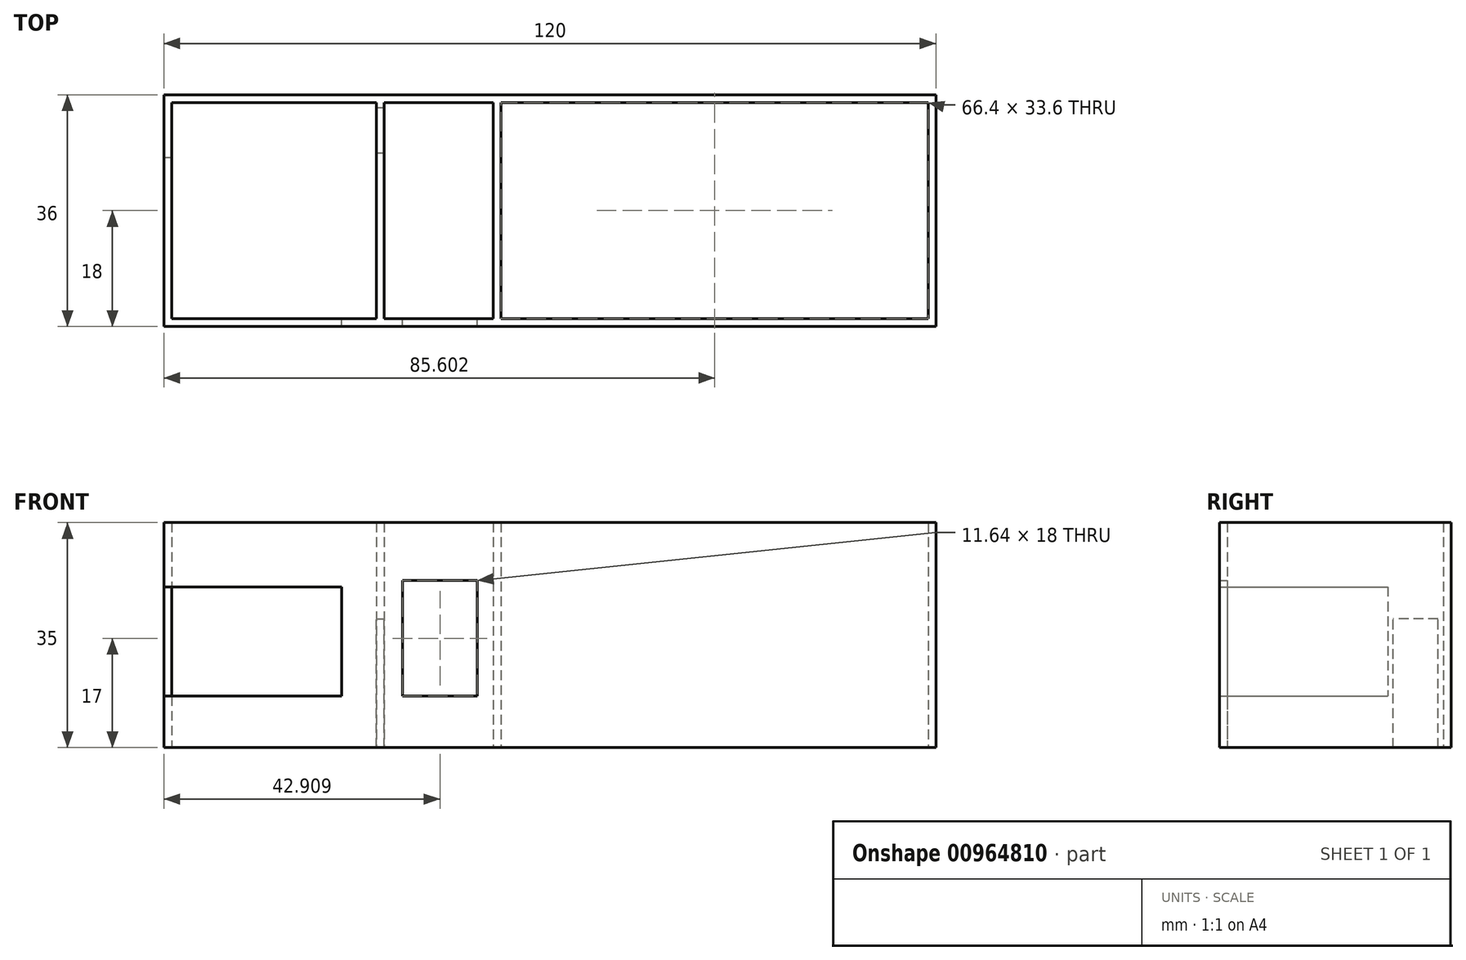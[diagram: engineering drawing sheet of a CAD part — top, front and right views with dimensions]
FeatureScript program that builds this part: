
annotation { "Feature Type Name" : "Feature", "Feature Type Description" : "" }
export const myFeature = defineFeature(function(context is Context, id is Id, definition is map)
    precondition{}
    {
        {
            var Q0;
            Q0=qCreatedBy(makeId("Top.planeOp"),FACE);
            var sketch = newSketch(context, id + "F0", { "sketchPlane" : qUnion([Q0])});
            skLineSegment(sketch, "E0.bottom", {"start": v(-115.18, 0) * mm, "end": v(4.82, 0) * mm});
            skLineSegment(sketch, "E0.top", {"start": v(-115.18, -36) * mm, "end": v(4.82, -36) * mm});
            skLineSegment(sketch, "E0.left", {"start": v(-115.18, 0) * mm, "end": v(-115.18, -36) * mm});
            skLineSegment(sketch, "E0.right", {"start": v(4.82, 0) * mm, "end": v(4.82, -36) * mm});
            skLineSegment(sketch, "E1.bottom", {"start": v(-113.98, -1.2) * mm, "end": v(3.62, -1.2) * mm});
            skLineSegment(sketch, "E1.top", {"start": v(-113.98, -34.8) * mm, "end": v(3.62, -34.8) * mm});
            skLineSegment(sketch, "E1.left", {"start": v(-113.98, -1.2) * mm, "end": v(-113.98, -34.8) * mm});
            skLineSegment(sketch, "E1.right", {"start": v(3.62, -1.2) * mm, "end": v(3.62, -34.8) * mm});
            skLineSegment(sketch, "E2.top", {"start": v(-63.98, -34.8) * mm, "end": v(-62.78, -34.8) * mm});
            skLineSegment(sketch, "E2.left", {"start": v(-63.98, -1.2) * mm, "end": v(-63.98, -34.8) * mm});
            skLineSegment(sketch, "E2.right", {"start": v(-62.78, -1.2) * mm, "end": v(-62.78, -34.8) * mm});
            skLineSegment(sketch, "E3.bottom", {"start": v(-49.02, -1.2) * mm, "end": v(-45.24, -1.2) * mm});
            skLineSegment(sketch, "E4.top", {"start": v(-82.18, -34.8) * mm, "end": v(-80.98, -34.8) * mm});
            skLineSegment(sketch, "E4.left", {"start": v(-82.18, -1.2) * mm, "end": v(-82.18, -34.8) * mm});
            skLineSegment(sketch, "E4.right", {"start": v(-80.98, -1.2) * mm, "end": v(-80.98, -34.8) * mm});
            skLineSegment(sketch, "E5.right", {"start": v(-82.18, -8.7) * mm, "end": v(-82.18, -26.7) * mm});
            skPoint(sketch, "E6", {"position": v(-80.98, -7.2) * mm});
            skPoint(sketch, "E7", {"position": v(-82.18, -7.2) * mm});
            skLineSegment(sketch, "E8.bottom", {"start": v(-107.98, -1.2) * mm, "end": v(-89.98, -1.2) * mm});
            skLineSegment(sketch, "E8.top", {"start": v(-107.98, -21.2) * mm, "end": v(-89.98, -21.2) * mm});
            skLineSegment(sketch, "E8.left", {"start": v(-107.98, -1.2) * mm, "end": v(-107.98, -21.2) * mm});
            skLineSegment(sketch, "E8.right", {"start": v(-89.98, -1.2) * mm, "end": v(-89.98, -21.2) * mm});
            skLineSegment(sketch, "E9.bottom", {"start": v(-80.98, -1.2) * mm, "end": v(-63.98, -1.2) * mm});
            skLineSegment(sketch, "E9.left", {"start": v(-80.98, -1.2) * mm, "end": v(-80.98, -8.13) * mm});
            skLineSegment(sketch, "E9.right", {"start": v(-63.98, -1.2) * mm, "end": v(-63.98, -8.13) * mm});
            skLineSegment(sketch, "E10.bottom", {"start": v(-80.98, -26.64) * mm, "end": v(-63.98, -26.64) * mm});
            skLineSegment(sketch, "E10.top", {"start": v(-80.98, -34.8) * mm, "end": v(-63.98, -34.8) * mm});
            skLineSegment(sketch, "E10.left", {"start": v(-80.98, -26.64) * mm, "end": v(-80.98, -34.8) * mm});
            skLineSegment(sketch, "E10.right", {"start": v(-63.98, -26.64) * mm, "end": v(-63.98, -34.8) * mm});
            skSolve(sketch);
        }
        {
            var Q0;
            Q0=makeQuery(id+"F0.imprint","IMPRINT",FACE,{"disambiguationData":[TD([[makeQuery(id+"F0.imprint","IMPRINT",EDGE,{"derivedFrom":sQuery(id+"F0.wireOp",EDGE,"E0.bottom")}),-1.0]])]});
            var Q1;
            {var subQ0=sQuery(id+"F0.wireOp",EDGE,"E4.left");var subQ4=makeQuery(id+"F0.imprint","IMPRINT",VERTEX,{"disambiguationData":[OD(0.0)],"derivedFrom":subQ0});Q1=makeQuery(id+"F0.imprint","IMPRINT",FACE,{"disambiguationData":[TD([[makeQuery(id+"F0.imprint","IMPRINT",EDGE,{"disambiguationData":[TD([[subQ4,-1.0]])],"derivedFrom":subQ0}),1.0]])]});}
            var Q2;
            {var subQ5=sQuery(id+"F0.wireOp",EDGE,"E2.right");Q2=makeQuery(id+"F0.imprint","IMPRINT",FACE,{"disambiguationData":[TD([[makeQuery(id+"F0.imprint","IMPRINT",EDGE,{"derivedFrom":subQ5}),-1.0]])]});}
            extrude(context, id + "F1", {"entities" : qUnion([Q0, Q1, Q2]), "depth" : 35 * mm, "offsetDistance" : 25 * mm});
        }
        {
            var Q0;
            Q0=makeQuery(id+"F1.opExtrude","SWEPT_FACE",FACE,{"disambiguationData":[OSD([sQuery(id+"F0.wireOp",EDGE,"E4.right")])]});
            var sketch = newSketch(context, id + "F2", { "sketchPlane" : qUnion([Q0])});
            skLineSegment(sketch, "E11.bottom", {"start": v(-2, 0) * mm, "end": v(-9, 0) * mm});
            skLineSegment(sketch, "E11.top", {"start": v(-2, 20) * mm, "end": v(-9, 20) * mm});
            skLineSegment(sketch, "E11.left", {"start": v(-2, 0) * mm, "end": v(-2, 20) * mm});
            skLineSegment(sketch, "E11.right", {"start": v(-9, 0) * mm, "end": v(-9, 20) * mm});
            skSolve(sketch);
        }
        {
            var Q0;
            Q0=makeQuery(id+"F2.imprint","IMPRINT",FACE,{"disambiguationData":[TD([[makeQuery(id+"F2.imprint","IMPRINT",EDGE,{"derivedFrom":sQuery(id+"F2.wireOp",EDGE,"E11.bottom")}),-1.0]])]});
            extrude(context, id + "F3", {"entities" : qUnion([Q0]), "operationType" : NewBodyOperationType.REMOVE, "oppositeDirection" : true, "depth" : 1.2 * mm, "offsetDistance" : 25 * mm});
        }
        {
            var Q0;
            {var subQ0=sQuery(id+"F0.wireOp",EDGE,"E1.top");Q0=makeQuery(id+"F1.opExtrude","SWEPT_FACE",FACE,{"disambiguationData":[OSD([subQ0]),TDD([makeQuery(id+"F0.imprint","IMPRINT",EDGE,{"disambiguationData":[TD([[makeQuery(id+"F0.imprint","INTERSECT",VERTEX,{"derivedFrom":[subQ0,sQuery(id+"F0.wireOp",EDGE,"E4.right")]}),-1.0]])],"derivedFrom":subQ0})])]});}
            var sketch = newSketch(context, id + "F4", { "sketchPlane" : qUnion([Q0])});
            skLineSegment(sketch, "E12.bottom", {"start": v(66.45, 26) * mm, "end": v(78.1, 26) * mm});
            skLineSegment(sketch, "E12.top", {"start": v(66.45, 8) * mm, "end": v(78.1, 8) * mm});
            skLineSegment(sketch, "E12.left", {"start": v(66.45, 26) * mm, "end": v(66.45, 8) * mm});
            skLineSegment(sketch, "E12.right", {"start": v(78.1, 26) * mm, "end": v(78.1, 8) * mm});
            skSolve(sketch);
        }
        {
            var Q0;
            Q0 = qSketchRegion(id + "F4", true);
            extrude(context, id + "F5", {"entities" : qUnion([Q0]), "operationType" : NewBodyOperationType.REMOVE, "endBound" : BoundingType.THROUGH_ALL, "oppositeDirection" : true, "depth" : 1.2 * mm, "offsetDistance" : 25 * mm});
        }
        {
            var Q0;
            {var subQ0=sQuery(id+"F0.wireOp",EDGE,"E1.top");Q0=makeQuery(id+"F1.opExtrude","SWEPT_FACE",FACE,{"disambiguationData":[OSD([subQ0]),TDD([makeQuery(id+"F0.imprint","IMPRINT",EDGE,{"disambiguationData":[TD([[makeQuery(id+"F0.imprint","INTERSECT",VERTEX,{"derivedFrom":[subQ0,sQuery(id+"F0.wireOp",EDGE,"E1.left")]}),-1.0]])],"derivedFrom":subQ0})])]});}
            var sketch = newSketch(context, id + "F6", { "sketchPlane" : qUnion([Q0])});
            skLineSegment(sketch, "E13.bottom", {"start": v(87.54, 25) * mm, "end": v(112.54, 25) * mm});
            skLineSegment(sketch, "E13.top", {"start": v(87.54, 8) * mm, "end": v(112.54, 8) * mm});
            skLineSegment(sketch, "E13.left", {"start": v(87.54, 25) * mm, "end": v(87.54, 8) * mm});
            skLineSegment(sketch, "E13.right", {"start": v(112.54, 25) * mm, "end": v(112.54, 8) * mm});
            skSolve(sketch);
        }
        {
            var Q0;
            Q0=makeQuery(id+"F6.imprint","IMPRINT",FACE,{"disambiguationData":[TD([[makeQuery(id+"F6.imprint","IMPRINT",EDGE,{"derivedFrom":sQuery(id+"F6.wireOp",EDGE,"E13.bottom")}),-1.0]])]});
            extrude(context, id + "F7", {"entities" : qUnion([Q0]), "operationType" : NewBodyOperationType.REMOVE, "oppositeDirection" : true, "depth" : 1.2 * mm, "offsetDistance" : 25 * mm});
        }
        {
            var Q0;
            Q0=makeQuery(id+"F7.boolean.opBoolean","COPY",FACE,{"derivedFrom":makeQuery(id+"F7.opExtrude","SWEPT_FACE",FACE,{"disambiguationData":[OSD([sQuery(id+"F6.wireOp",EDGE,"E13.right")])]})});
            var sketch = newSketch(context, id + "F8", { "sketchPlane" : qUnion([Q0])});
            skLineSegment(sketch, "E14.bottom", {"start": v(-36, 25) * mm, "end": v(-34.8, 25) * mm});
            skLineSegment(sketch, "E14.top", {"start": v(-36, 8) * mm, "end": v(-34.8, 8) * mm});
            skLineSegment(sketch, "E14.left", {"start": v(-36, 25) * mm, "end": v(-36, 8) * mm});
            skLineSegment(sketch, "E14.right", {"start": v(-34.8, 25) * mm, "end": v(-34.8, 8) * mm});
            skSolve(sketch);
        }
        {
            var Q0;
            Q0=makeQuery(id+"F8.imprint","IMPRINT",FACE,{"disambiguationData":[TD([[makeQuery(id+"F8.imprint","IMPRINT",EDGE,{"derivedFrom":sQuery(id+"F8.wireOp",EDGE,"E14.bottom")}),-1.0]])]});
            extrude(context, id + "F9", {"entities" : qUnion([Q0]), "operationType" : NewBodyOperationType.REMOVE, "oppositeDirection" : true, "depth" : 3 * mm, "offsetDistance" : 25 * mm});
        }
        {
            var Q0;
            Q0=makeQuery(id+"F1.opExtrude","SWEPT_FACE",FACE,{"disambiguationData":[OSD([sQuery(id+"F0.wireOp",EDGE,"E0.left")])]});
            var sketch = newSketch(context, id + "F10", { "sketchPlane" : qUnion([Q0])});
            skLineSegment(sketch, "E15.bottom", {"start": v(34.8, 25) * mm, "end": v(9.8, 25) * mm});
            skLineSegment(sketch, "E15.top", {"start": v(34.8, 8) * mm, "end": v(9.8, 8) * mm});
            skLineSegment(sketch, "E15.left", {"start": v(34.8, 25) * mm, "end": v(34.8, 8) * mm});
            skLineSegment(sketch, "E15.right", {"start": v(9.8, 25) * mm, "end": v(9.8, 8) * mm});
            skSolve(sketch);
        }
        {
            var Q0;
            Q0=makeQuery(id+"F10.imprint","IMPRINT",FACE,{"disambiguationData":[TD([[makeQuery(id+"F10.imprint","IMPRINT",EDGE,{"derivedFrom":sQuery(id+"F10.wireOp",EDGE,"E15.bottom")}),1.0]])]});
            extrude(context, id + "F11", {"entities" : qUnion([Q0]), "operationType" : NewBodyOperationType.REMOVE, "oppositeDirection" : true, "depth" : 1.2 * mm, "offsetDistance" : 25 * mm});
        }
    });
